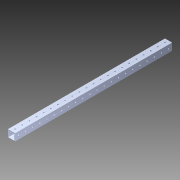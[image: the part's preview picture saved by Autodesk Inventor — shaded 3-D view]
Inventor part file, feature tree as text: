
AUTODESK INVENTOR PART (.ipt)
format: ipt  version: 2014 SP1 (Build 180222100, 222)  size: 1,209,856 bytes
history: native  units: in
note: dims shown in document units (in); Inventor stores cm internally (conversion verified against a paired STEP export)
features: pattern_circular x1, other x1, extrude x1, imported_body x1, sketch x1
ambient origin geometry x8: Origin, YZ Plane, XZ Plane, XY Plane, X Axis, Y Axis, Z Axis, Center Point
bodies: Body1 (feature_tree)
feature tree (5):
  pattern_circular  "CirPattern2"
  other  "1x1 tube1"
  extrude  "Extrusion1"  [1 undecoded]
  imported_body  "Base1"
  sketch  "Sketch1"  dims[d0=37.0in d1=0.0in]
note: 1 required parameter value undecoded (feature->parameter linkage not recoverable at this tier; creation-order binding heuristic only, values carry confidence <= 0.55)
